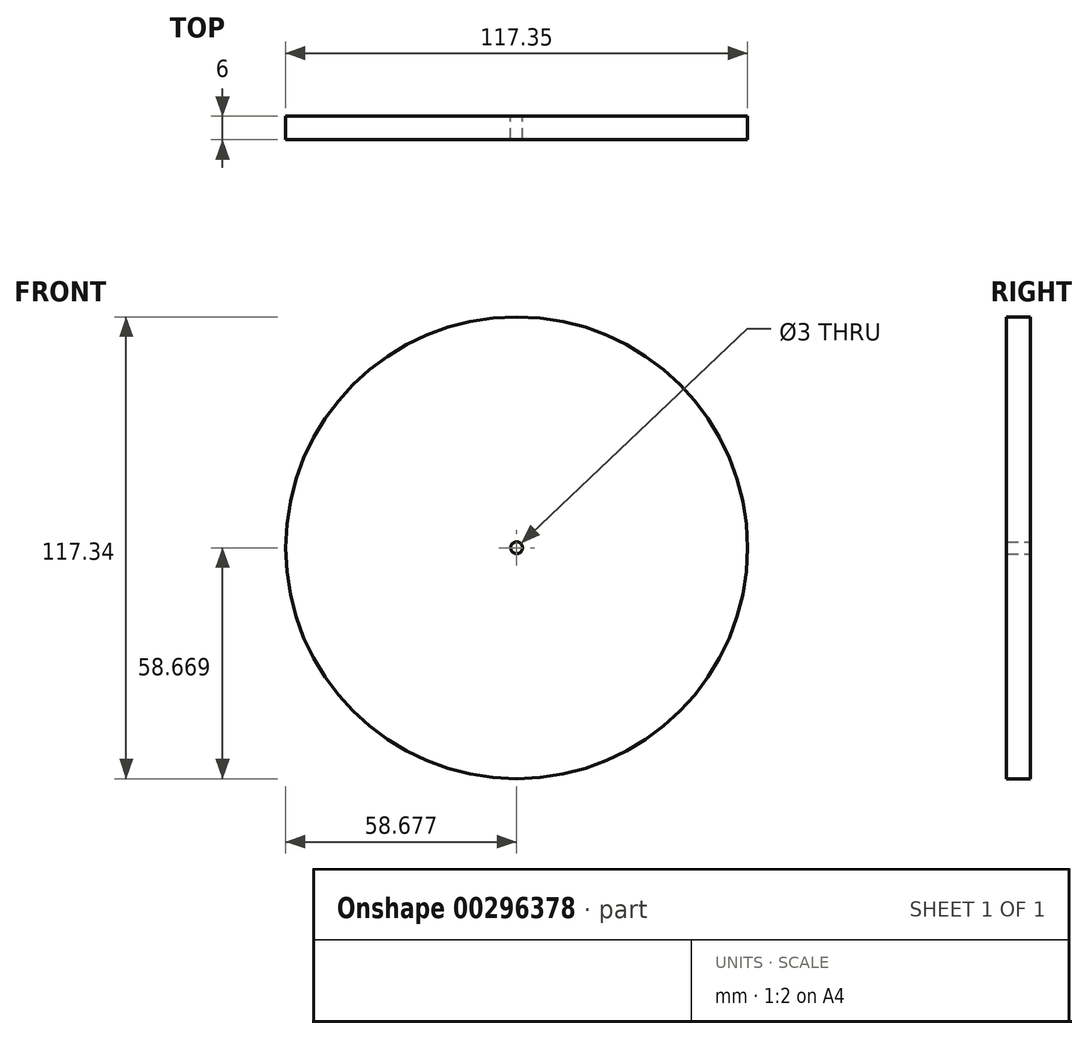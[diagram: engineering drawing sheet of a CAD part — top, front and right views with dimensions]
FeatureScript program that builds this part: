
annotation { "Feature Type Name" : "Feature", "Feature Type Description" : "" }
export const myFeature = defineFeature(function(context is Context, id is Id, definition is map)
    precondition{}
    {
        {
            var Q0;
            Q0=qCreatedBy(makeId("Front.planeOp"),FACE);
            var sketch = newSketch(context, id + "F0", { "sketchPlane" : qUnion([Q0])});
            skLineSegment(sketch, "E0", {"start": v(281.53, -100.1) * mm, "end": v(281.53, -140.1) * mm});
            skLineSegment(sketch, "E1", {"start": v(-318.47, 24.19) * mm, "end": v(-318.47, 76.33) * mm});
            skCircle(sketch, "E2", {"center": v(-145.86, -177.33) * mm, "radius": 58.67 * mm});
            skCircle(sketch, "E3", {"center": v(-145.86, -177.33) * mm, "radius": 1.5 * mm});
            skSolve(sketch);
        }
        {
            var Q0;
            Q0=makeQuery(id+"F0.imprint","IMPRINT",FACE,{"disambiguationData":[TD([[makeQuery(id+"F0.imprint","IMPRINT",EDGE,{"derivedFrom":sQuery(id+"F0.wireOp",EDGE,"E2")}),1.0]])]});
            extrude(context, id + "F1", {"entities" : qUnion([Q0]), "depth" : 6 * mm});
        }
    });
